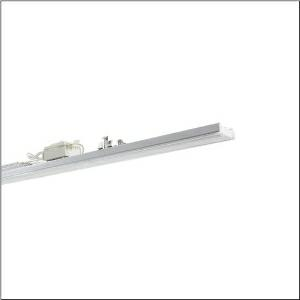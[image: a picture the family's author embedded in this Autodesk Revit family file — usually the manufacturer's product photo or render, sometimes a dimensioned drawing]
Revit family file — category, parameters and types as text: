
# Revit family: licross_r__11_recessed_ho_51tl18de465m_b9d1
name_source: partatom
category: Lighting Fixtures
units: mm (PartAtom-declared; Revit-internal decimal feet)

## family parameters
Cut with Voids When Loaded = No
Host = Face
Light Source = No
Part Type = Normal
Room Calculation Point = No
Round Connector Dimension = Use Diameter
Shared = No

## types (1)
- --- (1 x LED, 6940 lm, 40.2 W, 4000K)
    Apparent Load = 40 VA
    CIE Flux Codes = 78 94 99 100 100
    Color Rendering = 80
    Color Temperature = 4000K
    Default Elevation = 1800 mm
    Description = Licross® 11 Recessed HO, luminaire insert, of sheet steel, coil coated, white, length: 750mm, width: 66mm, height: 67mm, LED rated luminous flux: 6.940lm, light colour: 840, control gear: DALI 2, with plug, 5-pole, with phase selection, mains connection: 220..240V, AC, 50/60Hz, rated input power: 40W, halogen-free wiring, primary light control with lens, of plastic, primary optical cover: cover, of PMMA, light emission: direct distribution, primary light characteristic: symmetric, protection rating (complete): IP40, insulation class (complete): insulation class I (protective earthing), certification: CE, ENEC, VDE, UKCA, protection symbol: D if used in an environment without relevant dust loads with corresponding accessories, impact resistance: IK06, permissible ambient temperature for indoor applications: -25..+35°C, corresponds to IFS (International Featured Standards) requirements for safety and quality in the food industry, reducing of maximum allowable ambient temperature of 5°C with ceiling mounting, LABS conformity tested according to VDMA 24364:2018-05, packaging unit: 1 piece
    Height = 58 mm
    Lamp = 1 x LED
    Lamp Light Flux = 6940 lm
    Lamp Power = 40.2 W
    Lamp count = 1
    Length = 750 mm
    Luminous efficacy = 173 lm/W
    Manufacturer = Siteco
    ModVariant = No
    Model = 51TL18DE465M
    Mounting Place = Ceiling
    Mounting Type = Pendant
    Number of Poles = 1
    OnlyDefault = Yes
    Power Factor = 1
    Product Name = Licross® 11 Recessed HO
    Product group = luminaire insert
    ProductGroupID = 902
    Protection Class = Protection class I
    Protection Degree = IP 40
    RLX_Detail_Level = 1
    RLX_Emergency_Light_Flux = 0 lm
    RLX_Emergency_Type = 0
    RLX_Emergency_Type_DB = No
    RlxData = <blob elided: 29233 chars, md5=f00bc6f5>
    Socket = socket
    Standby Power = 0 W
    System Light Flux = 6940 lm
    System Power = 40 W
    Type Comments = factory setting: luminous flux: 100 % | dim-lin: 254 | 522 mA
    Type Image = l_1296930.jpg
    URL = http://relux.com
    VarID = @adj_099238
    Voltage = 0 V
    Weight = 0.00 kg
    Width = 66 mm

## geometry (parser evidence)
native form markers: Blend x4, Sweep x10
no freeform markers — native parametric forms only
